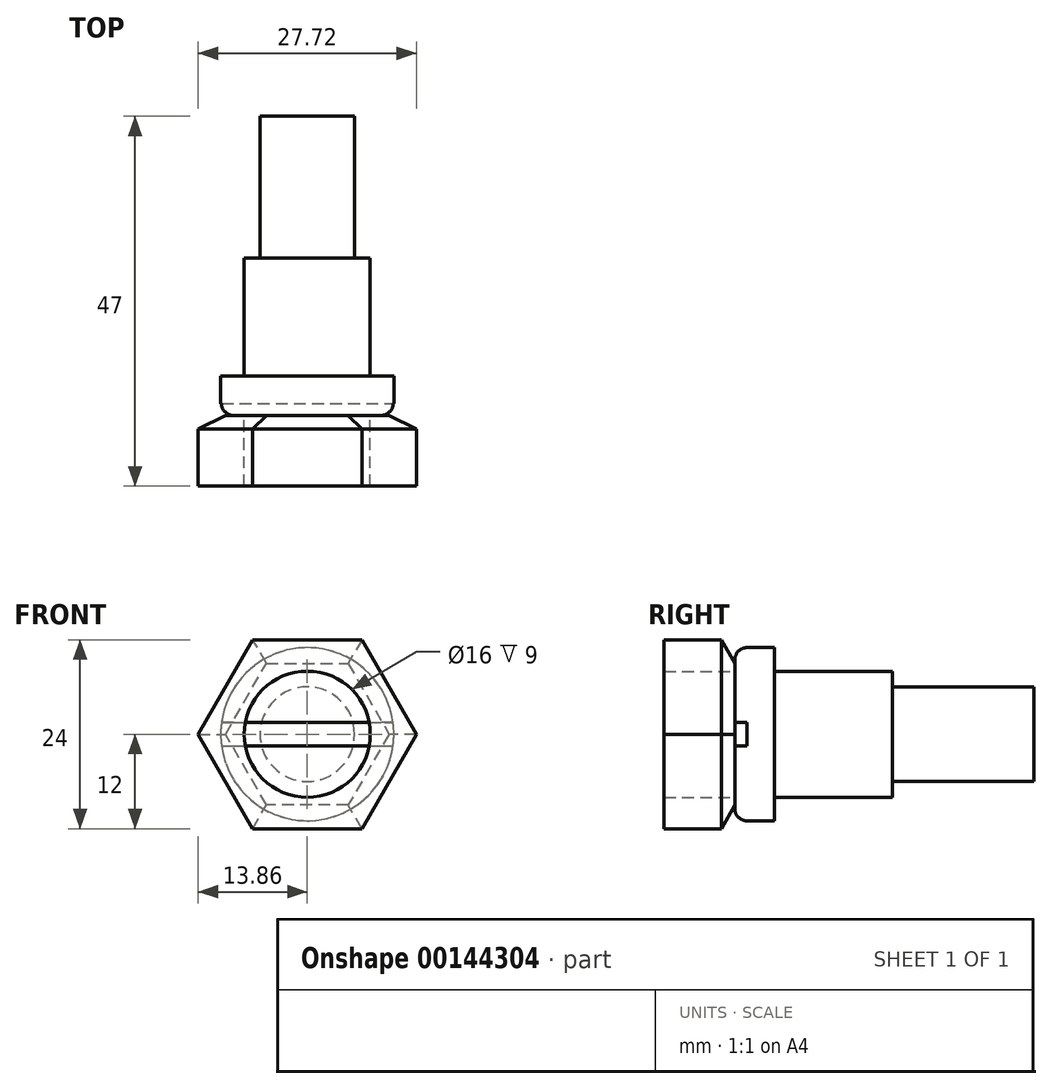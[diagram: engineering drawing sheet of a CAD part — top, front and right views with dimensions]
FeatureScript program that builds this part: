
annotation { "Feature Type Name" : "Feature", "Feature Type Description" : "" }
export const myFeature = defineFeature(function(context is Context, id is Id, definition is map)
    precondition{}
    {
        {
            var Q0;
            Q0=qCreatedBy(makeId("Right.planeOp"),FACE);
            var sketch = newSketch(context, id + "F0", { "sketchPlane" : qUnion([Q0])});
            skLineSegment(sketch, "E0", {"start": v(-23.21, 0) * mm, "end": v(51.1, 0) * mm, "construction": true});
            skLineSegment(sketch, "E1", {"start": v(0, 0) * mm, "end": v(0, 11) * mm});
            skLineSegment(sketch, "E2", {"start": v(0, 11) * mm, "end": v(5, 11) * mm});
            skLineSegment(sketch, "E3", {"start": v(5, 11) * mm, "end": v(5, 8) * mm});
            skLineSegment(sketch, "E4", {"start": v(5, 8) * mm, "end": v(20, 8) * mm});
            skLineSegment(sketch, "E5", {"start": v(20, 8) * mm, "end": v(20, 8) * mm});
            skLineSegment(sketch, "E6", {"start": v(38, 6) * mm, "end": v(38, 0) * mm});
            skLineSegment(sketch, "E7", {"start": v(38, 0) * mm, "end": v(0, 0) * mm});
            skLineSegment(sketch, "E8", {"start": v(20, 18.17) * mm, "end": v(20, -6.86) * mm, "construction": true});
            skPoint(sketch, "E9", {"position": v(20, 8) * mm});
            skLineSegment(sketch, "E10", {"start": v(38, 6) * mm, "end": v(20, 6) * mm});
            skLineSegment(sketch, "E11", {"start": v(20, 6) * mm, "end": v(20, 8) * mm});
            skSolve(sketch);
        }
        {
            var Q0;
            Q0=makeQuery(id+"F0.imprint","IMPRINT",FACE,{"disambiguationData":[TD([[makeQuery(id+"F0.imprint","IMPRINT",EDGE,{"derivedFrom":sQuery(id+"F0.wireOp",EDGE,"E1")}),-1.0]])]});
            var Q1;
            Q1=sQuery(id+"F0.wireOp",EDGE,"E0");
            revolve(context, id + "F1", {"entities" : qUnion([Q0]), "axis" : qUnion([Q1]), "revolveType" : RevolveType.FULL});
        }
        {
            var Q0;
            Q0=qCreatedBy(makeId("Front.planeOp"),FACE);
            var sketch = newSketch(context, id + "F2", { "sketchPlane" : qUnion([Q0])});
            skCircle(sketch, "E12.cCircle", {"center": v(0, 0) * mm, "radius": 12 * mm, "construction": true});
            skLineSegment(sketch, "E12.0", {"start": v(6.93, -12) * mm, "end": v(-6.93, -12) * mm});
            skLineSegment(sketch, "E12.1", {"start": v(-6.93, -12) * mm, "end": v(-13.86, 0) * mm});
            skLineSegment(sketch, "E12.2", {"start": v(-13.86, 0) * mm, "end": v(-6.93, 12) * mm});
            skLineSegment(sketch, "E12.3", {"start": v(-6.93, 12) * mm, "end": v(6.93, 12) * mm});
            skLineSegment(sketch, "E12.4", {"start": v(6.93, 12) * mm, "end": v(13.86, 0) * mm});
            skLineSegment(sketch, "E12.5", {"start": v(13.86, 0) * mm, "end": v(6.93, -12) * mm});
            skPoint(sketch, "E12.0.midPoint", {"position": v(0, -12) * mm});
            skCircle(sketch, "E13", {"center": v(0, 0) * mm, "radius": 8 * mm});
            skSolve(sketch);
        }
        {
            var Q0;
            Q0 = qSketchRegion(id + "F2", true);
            extrude(context, id + "F3", {"entities" : qUnion([Q0]), "depth" : 9 * mm});
        }
        {
            var Q0;
            Q0=makeQuery(id+"F1.opRevolve","SWEPT_FACE",FACE,{"disambiguationData":[OSD([sQuery(id+"F0.wireOp",EDGE,"E1")])]});
            var sketch = newSketch(context, id + "F4", { "sketchPlane" : qUnion([Q0])});
            skLineSegment(sketch, "E14.bottom", {"start": v(-12.04, 1.5) * mm, "end": v(12.96, 1.5) * mm});
            skLineSegment(sketch, "E14.top", {"start": v(-12.04, -1.5) * mm, "end": v(12.96, -1.5) * mm});
            skLineSegment(sketch, "E14.left", {"start": v(-12.04, 1.5) * mm, "end": v(-12.04, -1.5) * mm});
            skLineSegment(sketch, "E14.right", {"start": v(12.96, 1.5) * mm, "end": v(12.96, -1.5) * mm});
            skSolve(sketch);
        }
        {
            var Q0;
            Q0 = qSketchRegion(id + "F4", true);
            extrude(context, id + "F5", {"entities" : qUnion([Q0]), "operationType" : NewBodyOperationType.REMOVE, "oppositeDirection" : true, "depth" : 1.5 * mm});
        }
        {
            var Q0;
            {var subQ0=sQuery(id+"F0.wireOp",EDGE,"E1");var subQ1=sQuery(id+"F0.wireOp",EDGE,"E2");Q0=makeQuery(id+"F5.boolean.opBoolean","SPLIT",EDGE,{"disambiguationData":[TD([makeQuery(id+"F5.opExtrude","SWEPT_FACE",FACE,{"disambiguationData":[OSD([sQuery(id+"F4.wireOp",EDGE,"E14.bottom")])]})])],"derivedFrom":makeQuery(id+"F1.opRevolve","SWEPT_EDGE",EDGE,{"disambiguationData":[OSD([subQ0,subQ1])]})});}
            var Q1;
            {var subQ0=sQuery(id+"F0.wireOp",EDGE,"E1");var subQ1=sQuery(id+"F0.wireOp",EDGE,"E2");Q1=makeQuery(id+"F5.boolean.opBoolean","SPLIT",EDGE,{"disambiguationData":[TD([makeQuery(id+"F5.opExtrude","SWEPT_FACE",FACE,{"disambiguationData":[OSD([sQuery(id+"F4.wireOp",EDGE,"E14.top")])]})])],"derivedFrom":makeQuery(id+"F1.opRevolve","SWEPT_EDGE",EDGE,{"disambiguationData":[OSD([subQ0,subQ1])]})});}
            fillet(context, id + "F6", {"entities" : qUnion([Q0, Q1]), "radius" : 1.5 * mm, "tangentPropagation" : true, "allowEdgeOverflow" : false});
        }
        {
            var Q0;
            Q0=makeQuery(id+"F3.opExtrude","CAP_EDGE",EDGE,{"disambiguationData":[OSD([sQuery(id+"F2.wireOp",EDGE,"E12.3")])],"isStart":true});
            var Q1;
            Q1=makeQuery(id+"F3.opExtrude","CAP_EDGE",EDGE,{"disambiguationData":[OSD([sQuery(id+"F2.wireOp",EDGE,"E12.4")])],"isStart":true});
            var Q2;
            Q2=makeQuery(id+"F3.opExtrude","CAP_EDGE",EDGE,{"disambiguationData":[OSD([sQuery(id+"F2.wireOp",EDGE,"E12.5")])],"isStart":true});
            var Q3;
            Q3=makeQuery(id+"F3.opExtrude","CAP_EDGE",EDGE,{"disambiguationData":[OSD([sQuery(id+"F2.wireOp",EDGE,"E12.0")])],"isStart":true});
            var Q4;
            Q4=makeQuery(id+"F3.opExtrude","CAP_EDGE",EDGE,{"disambiguationData":[OSD([sQuery(id+"F2.wireOp",EDGE,"E12.1")])],"isStart":true});
            var Q5;
            Q5=makeQuery(id+"F3.opExtrude","CAP_EDGE",EDGE,{"disambiguationData":[OSD([sQuery(id+"F2.wireOp",EDGE,"E12.2")])],"isStart":true});
            chamfer(context, id + "F7", {"entities" : qUnion([Q0, Q1, Q2, Q3, Q4, Q5]), "chamferType" : ChamferType.OFFSET_ANGLE, "width" : 3 * mm, "oppositeDirection" : false, "angle" : 30 * degree, "tangentPropagation" : true});
        }
    });
